# Revit family: 91105C6A 91106C6A care plus basin mixer HC – standard and care handle
name_source: partatom
category: Plumbing Fixtures
units: mm (PartAtom-declared; Revit-internal decimal feet)

## family parameters
Cut with Voids When Loaded = No
Host = Face
OmniClass Number = 23.45.55.17
OmniClass Title = Mixing Faucets
Part Type = Normal
Room Calculation Point = No
Round Connector Dimension = Use Radius
Shared = No

## types (2) — shared parameters
Assembly Code = C1030210
CW Connection = Yes
CWFU = 1.58
Connector Radius = 10 mm  [stored 0.0328084 ft]
HW Connection = Yes
HWFU = 1.58
Height_ANZRS = 156 mm
Length_ANZRS = 46 mm
Manufacturer = GWA Bathrooms & Kitchens
Material_ANZRS = Metal-Chrome-Caroma
ModifiedIssue_ANZRS = 2022.01 $
URL = https://specify.caroma.com.au
Vent Connection = No
WELSRating_ANZRS = WELS 6 Star rated, 4.5L/min
Waste Connection = No
zero-valued in all types: Cost, Default Elevation

## per-type parameters (varying)
| type | Care Lever | Description | Model | Standard Lever | Type Comments | Width_ANZRS |
| 91105C6A care plus basin mixer standard handle HC (hot / cold) | No | Care Plus Basin Mixer standard handle HC (hot / cold) | 91105C6A | Yes | Care Plus Basin Mixer standard handle HC (hot / cold) | 161 mm |
| 91106C6A care plus basin mixer care handle HC (hot / cold) | Yes | Care Plus Basin Mixer care handle HC (hot / cold) | 91106C6A | No | Care Plus Basin Mixer care handle HC (hot / cold) | 240 mm |

note: [stored X ft] marks values corroborated as IEEE doubles in the binary element streams (Revit-internal decimal feet)

## geometry (parser evidence)
native form markers: Blend x2, Sweep x2
no freeform markers — native parametric forms only
